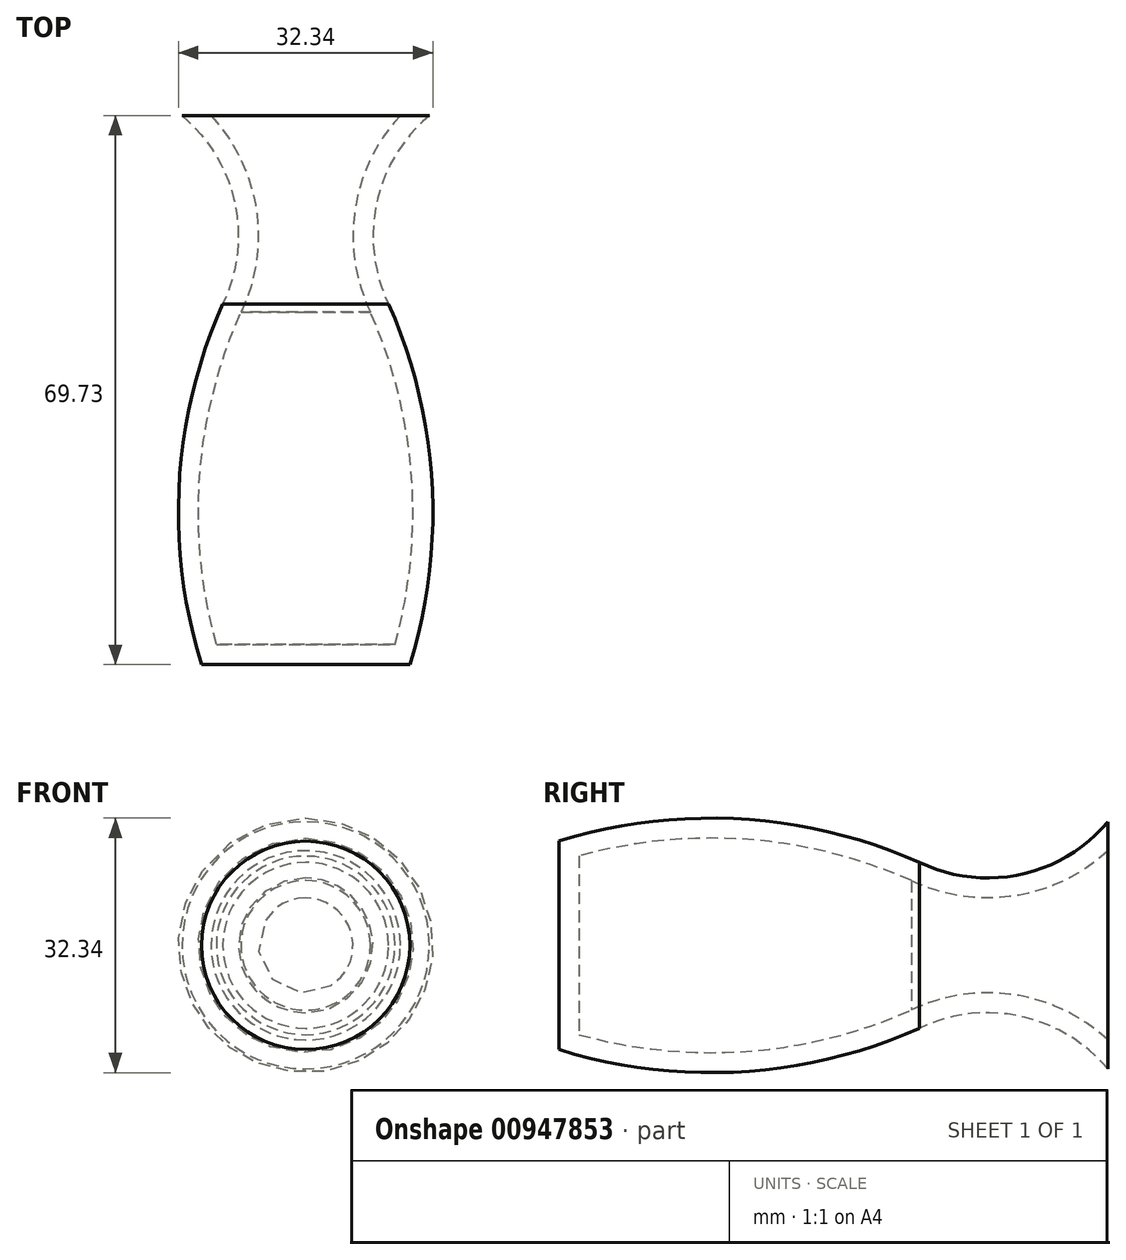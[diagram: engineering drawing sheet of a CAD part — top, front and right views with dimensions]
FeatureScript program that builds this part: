
annotation { "Feature Type Name" : "Feature", "Feature Type Description" : "" }
export const myFeature = defineFeature(function(context is Context, id is Id, definition is map)
    precondition{}
    {
        {
            var Q0;
            Q0=qCreatedBy(makeId("Top.planeOp"),FACE);
            var sketch = newSketch(context, id + "F0", { "sketchPlane" : qUnion([Q0])});
            skLineSegment(sketch, "E0", {"start": v(0, 38.17) * mm, "end": v(0, -31.56) * mm});
            skLineSegment(sketch, "E1", {"start": v(0, -31.56) * mm, "end": v(-13.24, -31.56) * mm});
            skArc(sketch, "E2", {"start": v(-10.53, 14.26) * mm, "mid": v(-16.05, -8.4) * mm, "end": v(-13.24, -31.56) * mm});
            skArc(sketch, "E3", {"start": v(-10.53, 14.26) * mm, "mid": v(-9.01, 27.1) * mm, "end": v(-15.7, 38.17) * mm});
            skLineSegment(sketch, "E4", {"start": v(-15.7, 38.17) * mm, "end": v(0, 38.17) * mm});
            skSolve(sketch);
        }
        {
            var Q0;
            Q0=makeQuery(id+"F0.imprint","IMPRINT",FACE,{"disambiguationData":[TD([[makeQuery(id+"F0.imprint","IMPRINT",EDGE,{"derivedFrom":sQuery(id+"F0.wireOp",EDGE,"E0")}),-1.0]])]});
            var Q1;
            Q1=sQuery(id+"F0.wireOp",EDGE,"E0");
            revolve(context, id + "F1", {"surfaceOperationType" : NewSurfaceOperationType.NEW, "entities" : qUnion([Q0]), "axis" : qUnion([Q1]), "revolveType" : RevolveType.FULL});
        }
        {
            var Q0;
            Q0=makeQuery(id+"F1.opRevolve","SWEPT_FACE",FACE,{"disambiguationData":[OSD([sQuery(id+"F0.wireOp",EDGE,"E4")])]});
            shell(context, id + "F2", {"entities" : qUnion([Q0]), "thickness" : 2.54 * mm});
        }
    });
